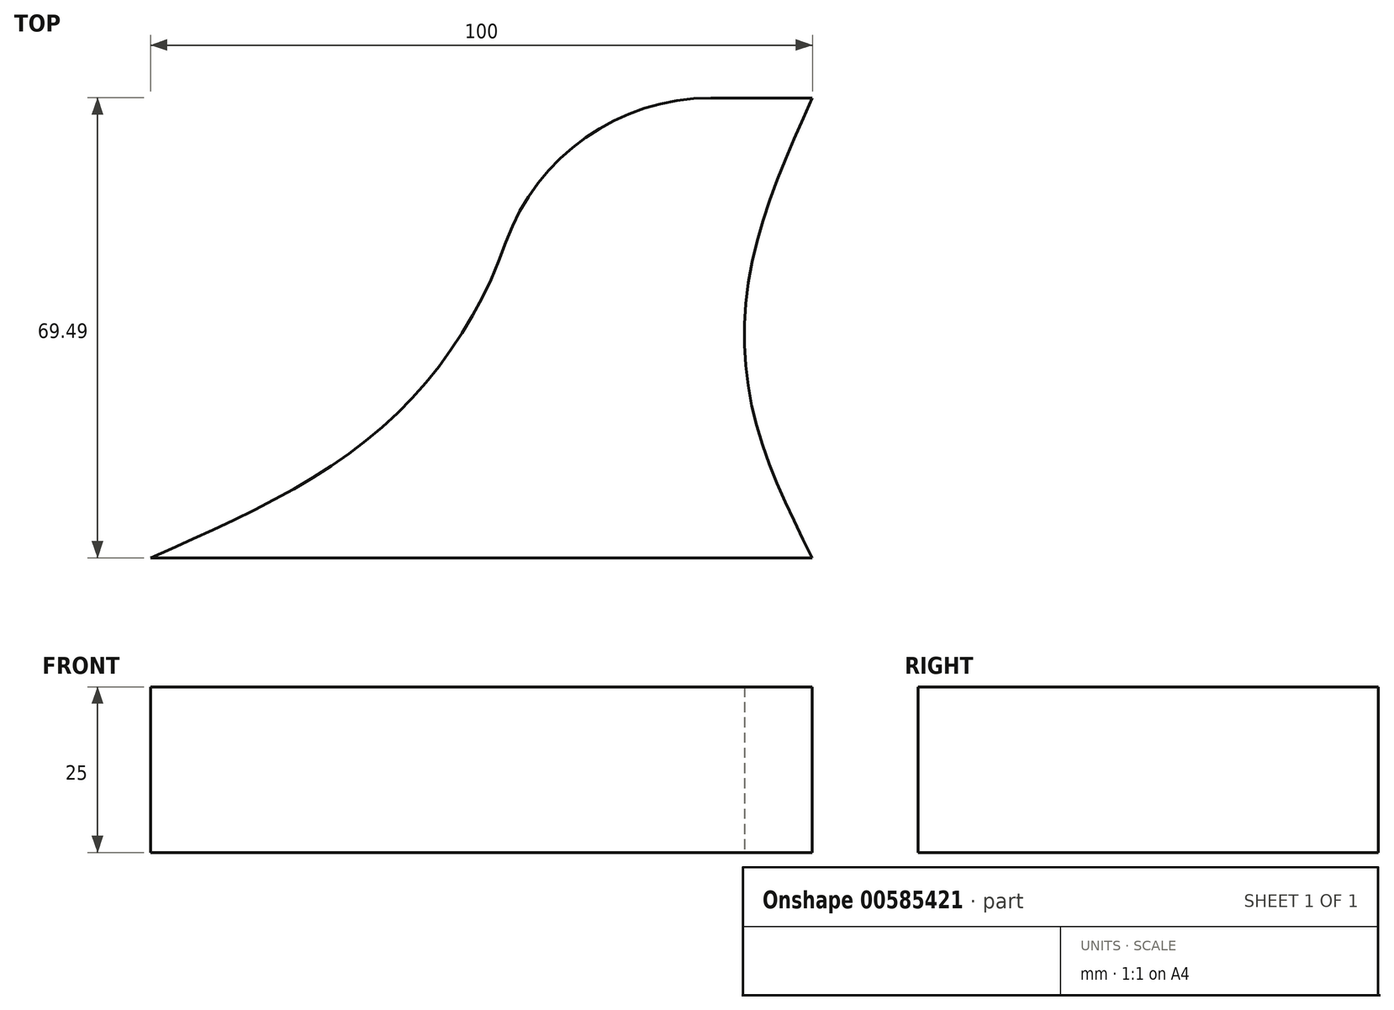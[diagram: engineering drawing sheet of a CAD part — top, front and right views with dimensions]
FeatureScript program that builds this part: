
annotation { "Feature Type Name" : "Feature", "Feature Type Description" : "" }
export const myFeature = defineFeature(function(context is Context, id is Id, definition is map)
    precondition{}
    {
        {
            var Q0;
            Q0=qCreatedBy(makeId("Top.planeOp"),FACE);
            var sketch = newSketch(context, id + "F0", { "sketchPlane" : qUnion([Q0])});
            skLineSegment(sketch, "E0", {"start": v(-39.23, 0) * mm, "end": v(60.77, 0) * mm});
            skLineSegment(sketch, "E1", {"start": v(52.75, 69.49) * mm, "end": v(20.25, 69.49) * mm});
            skFitSpline(sketch, "E2", {"points": [v(-39.23, 0) * mm, v(-7.26, 17.21) * mm, v(11.72, 41) * mm, v(20.25, 69.49) * mm], "startDerivative": vector(96.76, 42.75) * mm, "endDerivative": vector(20.18, 91.3) * mm});
            skFitSpline(sketch, "E3", {"points": [v(60.77, 0) * mm, v(51.94, 21.46) * mm, v(51.66, 44.69) * mm, v(60.77, 69.49) * mm], "startDerivative": vector(-32.3, 64.4) * mm, "endDerivative": vector(31.8, 70.95) * mm});
            skLineSegment(sketch, "E4", {"start": v(60.77, 69.49) * mm, "end": v(52.75, 69.49) * mm});
            skSolve(sketch);
        }
        {
            var Q0;
            Q0 = qSketchRegion(id + "F0", true);
            extrude(context, id + "F1", {"entities" : qUnion([Q0]), "depth" : 25 * mm, "offsetDistance" : 25 * mm});
        }
        {
            var Q0;
            Q0=makeQuery(id+"F1.opExtrude","SWEPT_EDGE",EDGE,{"disambiguationData":[OSD([sQuery(id+"F0.wireOp",EDGE,"E1"),sQuery(id+"F0.wireOp",EDGE,"E2")])]});
            fillet(context, id + "F2", {"entities" : qUnion([Q0]), "radius" : 32.9 * mm, "tangentPropagation" : true, "allowEdgeOverflow" : false});
        }
    });
